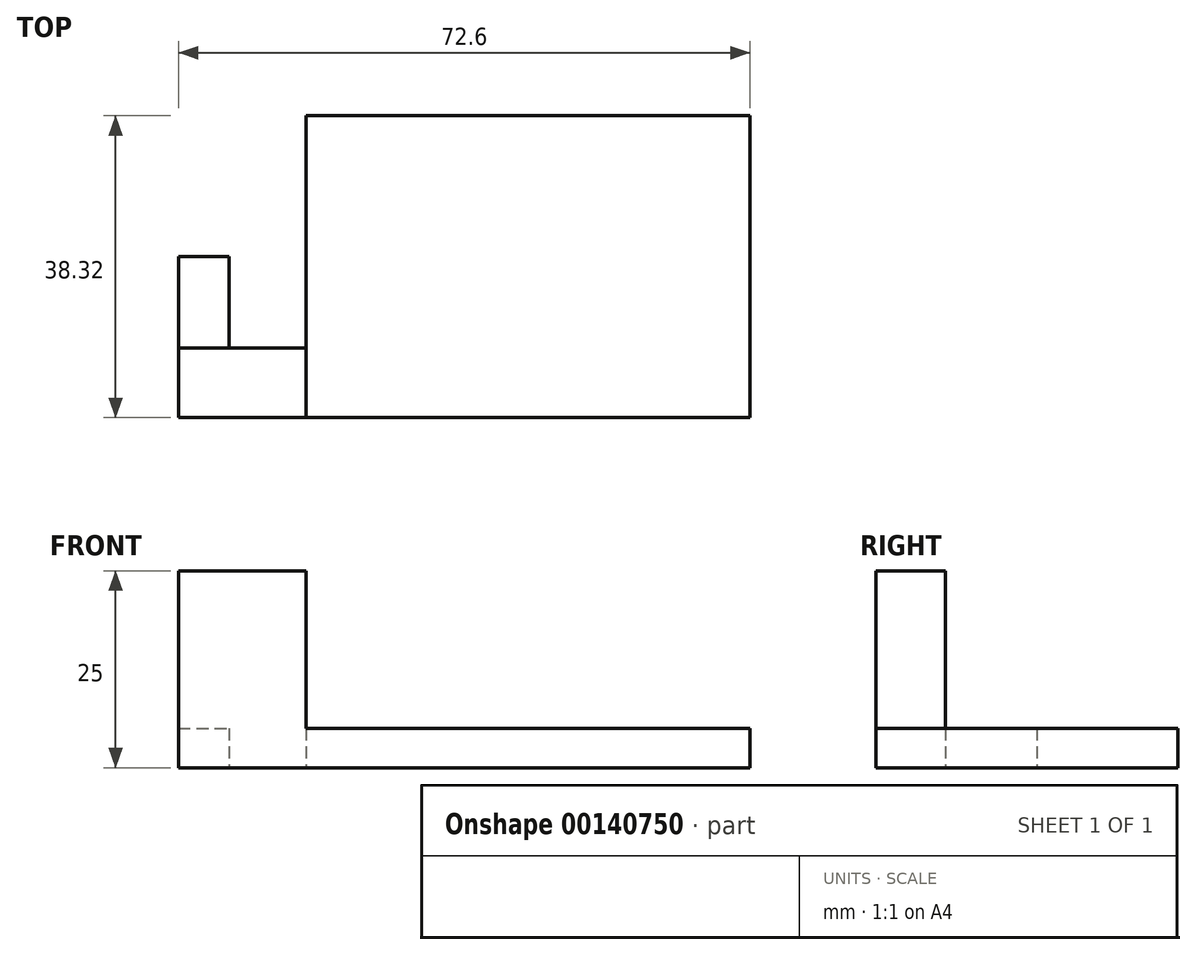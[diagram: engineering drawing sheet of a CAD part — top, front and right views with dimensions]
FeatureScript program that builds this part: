
annotation { "Feature Type Name" : "Feature", "Feature Type Description" : "" }
export const myFeature = defineFeature(function(context is Context, id is Id, definition is map)
    precondition{}
    {
        {
            var Q0;
            Q0=qCreatedBy(makeId("Top.planeOp"),FACE);
            var sketch = newSketch(context, id + "F0", { "sketchPlane" : qUnion([Q0])});
            skLineSegment(sketch, "E0.bottom", {"start": v(0, 0) * mm, "end": v(56.4, 0) * mm});
            skLineSegment(sketch, "E0.top", {"start": v(0, 38.32) * mm, "end": v(56.4, 38.32) * mm});
            skLineSegment(sketch, "E0.left", {"start": v(0, 0) * mm, "end": v(0, 38.32) * mm});
            skLineSegment(sketch, "E0.right", {"start": v(56.4, 0) * mm, "end": v(56.4, 38.32) * mm});
            skLineSegment(sketch, "E1.bottom", {"start": v(0, 0) * mm, "end": v(12.42, 0) * mm});
            skLineSegment(sketch, "E1.top", {"start": v(0, 38.32) * mm, "end": v(12.42, 38.32) * mm});
            skLineSegment(sketch, "E1.right", {"start": v(12.42, 0) * mm, "end": v(12.42, 38.32) * mm});
            skLineSegment(sketch, "E2.bottom", {"start": v(0, 0) * mm, "end": v(-16.19, 0) * mm});
            skLineSegment(sketch, "E2.top", {"start": v(0, 8.84) * mm, "end": v(-16.19, 8.84) * mm});
            skLineSegment(sketch, "E2.left", {"start": v(0, 0) * mm, "end": v(0, 8.84) * mm});
            skLineSegment(sketch, "E2.right", {"start": v(-16.19, 0) * mm, "end": v(-16.19, 8.84) * mm});
            skLineSegment(sketch, "E3.bottom", {"start": v(-9.77, 8.84) * mm, "end": v(-16.19, 8.84) * mm});
            skLineSegment(sketch, "E3.top", {"start": v(-9.77, 20.46) * mm, "end": v(-16.19, 20.46) * mm});
            skLineSegment(sketch, "E3.left", {"start": v(-9.77, 8.84) * mm, "end": v(-9.77, 20.46) * mm});
            skLineSegment(sketch, "E3.right", {"start": v(-16.19, 8.84) * mm, "end": v(-16.19, 20.46) * mm});
            skSolve(sketch);
        }
        {
            var Q0;
            Q0 = qSketchRegion(id + "F0", true);
            extrude(context, id + "F1", {"entities" : qUnion([Q0]), "depth" : 5 * mm});
        }
        {
            var Q0;
            Q0=makeQuery(id+"F0.imprint","IMPRINT",FACE,{"disambiguationData":[TD([[makeQuery(id+"F0.imprint","IMPRINT",EDGE,{"derivedFrom":sQuery(id+"F0.wireOp",EDGE,"E1.bottom")}),1.0]])]});
            var Q1;
            Q1=makeQuery(id+"F0.imprint","IMPRINT",FACE,{"disambiguationData":[TD([[makeQuery(id+"F0.imprint","IMPRINT",EDGE,{"derivedFrom":sQuery(id+"F0.wireOp",EDGE,"E2.bottom")}),-1.0]])]});
            var Q2;
            Q2=makeQuery(id+"F0.imprint","IMPRINT",FACE,{"disambiguationData":[TD([[makeQuery(id+"F0.imprint","IMPRINT",EDGE,{"derivedFrom":sQuery(id+"F0.wireOp",EDGE,"E3.bottom")}),-1.0]])]});
            extrude(context, id + "F2", {"entities" : qUnion([Q0, Q1, Q2]), "operationType" : NewBodyOperationType.ADD, "depth" : 25 * mm});
        }
    });
